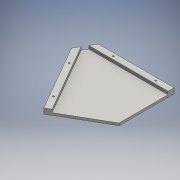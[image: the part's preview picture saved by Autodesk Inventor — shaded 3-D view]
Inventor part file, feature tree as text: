
AUTODESK INVENTOR PART (.ipt)
format: ipt  version: 2016 SP1 (Build 200210100, 210)  size: 235,008 bytes
history: native  units: mm
features: extrude x3, sketch x3, reference x1, projected_geometry x1
ambient origin geometry x8: Origin, YZ Plane, XZ Plane, XY Plane, X Axis, Y Axis, Z Axis, Center Point
bodies: Solid1 (feature_tree)
feature tree (8):
  extrude  "Extrusion1"  Depth=20.0mm
  extrude  "Extrusion2"  Depth=10.0mm
  extrude  "Extrusion3"  Depth=10.0mm
  sketch  "Sketch1"  dims[d0=18.0mm d1=0.0mm d2=20.0mm]
  reference  "Reference1"
  sketch  "Sketch2"  dims[d3=10.0mm d4=0.0mm d5=5.0mm]
  projected_geometry  "Projected Loop1"
  sketch  "Sketch3"  dims[d6=5.0mm d7=5.0mm d8=5.0mm d9=10.0mm d10=10.0mm d11=50.0mm d12=190.0mm d13=10.0mm d14=10.0mm d15=50.0mm d16=190.0mm d17=10.0mm d18=0.0mm]
